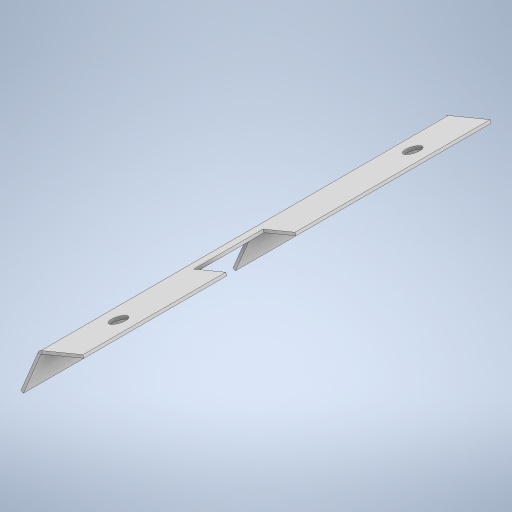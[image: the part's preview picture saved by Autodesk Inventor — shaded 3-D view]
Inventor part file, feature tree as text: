
AUTODESK INVENTOR PART (.ipt)
format: ipt  version: 2024.2 (Build 282272000, 272)  size: 401,408 bytes
history: native  units: mm
features: sketch x6, extrude x5, sheet_metal_op x3, pattern_linear x2, other x2
ambient origin geometry x8: Origin, YZ Plane, XZ Plane, XY Plane, X Axis, Y Axis, Z Axis, Center Point
bodies: Body1 (feature_tree)
feature tree (18):
  sheet_metal_op  "Contour Flange1"
  extrude  "Extrusion1"  Depth=3.0mm
  extrude  "Extrusion5"  Depth=4.0mm
  extrude  "Extrusion6"  Depth=2.0mm
  pattern_linear  "Rectangular Pattern4"  Spacing1=2006.0mm  [1 undecoded]
  extrude  "Extrusion7"  Depth=2.0mm
  pattern_linear  "Rectangular Pattern5"  Spacing1=3.0mm  [1 undecoded]
  extrude  "Extrusion8"  Depth=293.75mm
  sketch  "Sketch4"  dims[d16=506.0mm d22=3.0mm]
  other  "Plate3"
  sheet_metal_op  "Bend2"
  sheet_metal_op  "Corner2"
  sketch  "Sketch6"  dims[d23=32.642mm d24=4.0mm]
  sketch  "Sketch10"  dims[d25=2.0mm d26=2.0mm]
  sketch  "Sketch12"  dims[d27=1.0mm]
  sketch  "Sketch13"  dims[d28=4.0mm]
  sketch  "Sketch14"  dims[d29=2.0mm d30=2006.0mm d31=2.0mm d32=3.0mm d33=8.0mm d34=2.0mm d35=2.0mm d36=11.0mm d37=40.75mm d40=40.75mm d41=11.0mm d42=10.0mm d43=0.0mm d70=50.0mm d71=25.0mm d72=125.0mm d73=0.0mm d74=0.0mm d75=50.0mm d76=25.0mm d77=125.0mm d78=0.0mm d79=0.0mm d80=80.0mm d82=250.0mm d83=11.0mm d84=0.0mm d85=0.0mm d86=70.0mm d88=250.0mm d89=600.0mm d90=1712.25mm d91=600.0mm d92=0.0mm d94=293.75mm d95=293.75mm]
  other  "Definition1"
note: 2 required parameter values undecoded (feature->parameter linkage not recoverable at this tier; creation-order binding heuristic only, values carry confidence <= 0.55)
